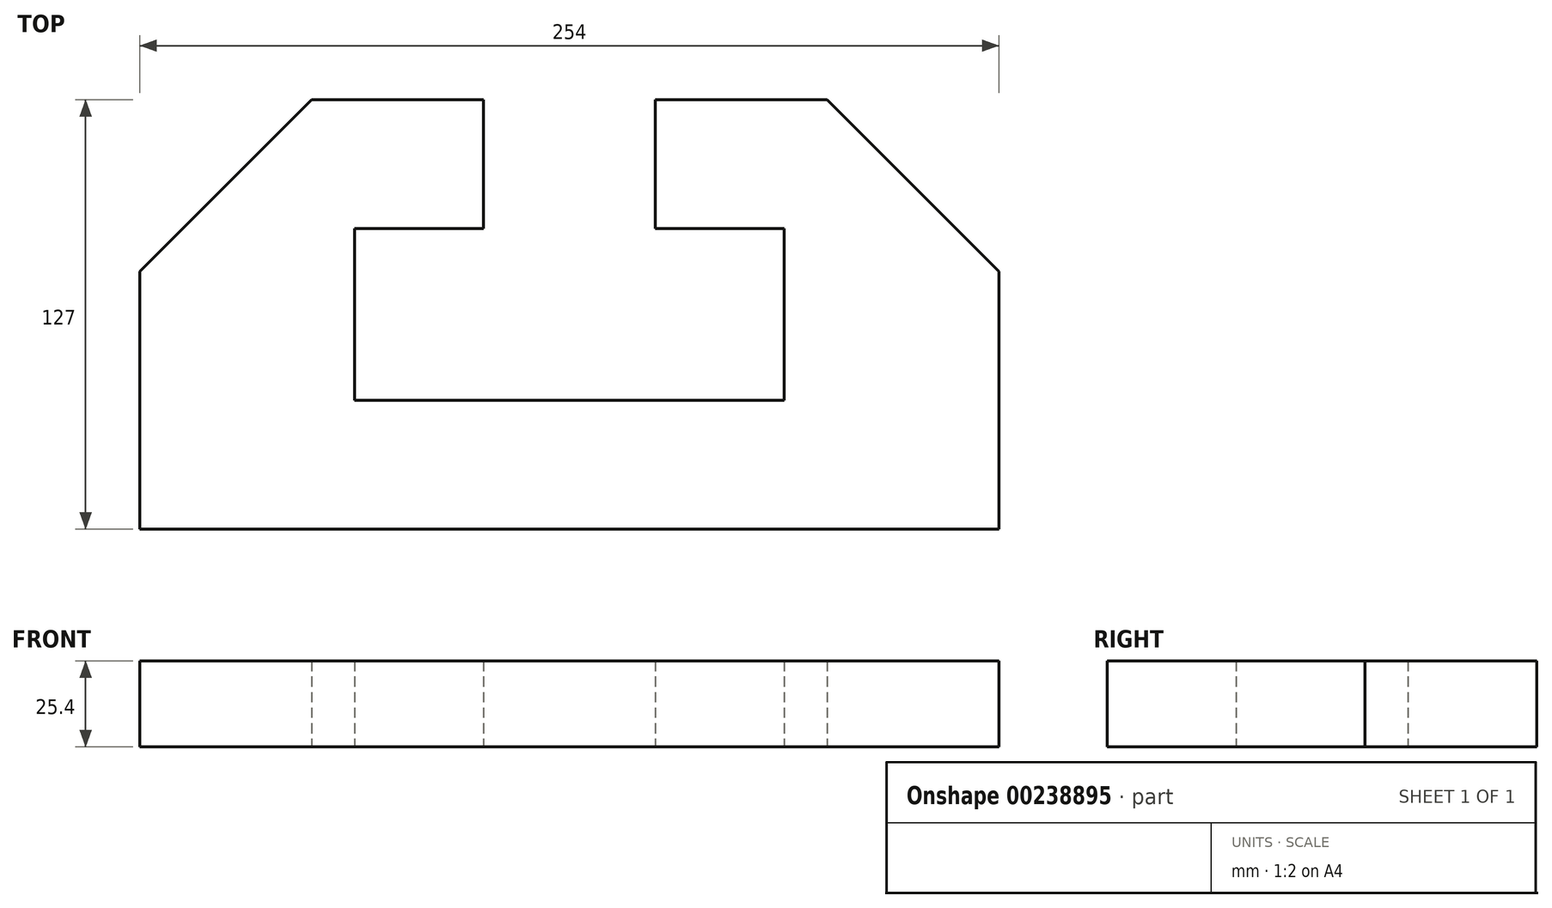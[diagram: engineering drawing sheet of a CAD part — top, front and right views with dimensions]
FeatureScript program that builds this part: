
annotation { "Feature Type Name" : "Feature", "Feature Type Description" : "" }
export const myFeature = defineFeature(function(context is Context, id is Id, definition is map)
    precondition{}
    {
        {
            var Q0;
            Q0=qCreatedBy(makeId("Top.planeOp"),FACE);
            var sketch = newSketch(context, id + "F0", { "sketchPlane" : qUnion([Q0])});
            skLineSegment(sketch, "E0", {"start": v(-152.4, -88.9) * mm, "end": v(101.6, -88.9) * mm});
            skLineSegment(sketch, "E1", {"start": v(-152.4, -88.9) * mm, "end": v(-152.4, -12.7) * mm});
            skLineSegment(sketch, "E2", {"start": v(-152.4, -12.7) * mm, "end": v(-101.6, 38.1) * mm});
            skLineSegment(sketch, "E3", {"start": v(-101.6, 38.1) * mm, "end": v(-50.8, 38.1) * mm});
            skLineSegment(sketch, "E4", {"start": v(-50.8, 38.1) * mm, "end": v(-50.8, 0) * mm});
            skLineSegment(sketch, "E5", {"start": v(-50.8, 0) * mm, "end": v(-88.9, 0) * mm});
            skLineSegment(sketch, "E6", {"start": v(-88.9, 0) * mm, "end": v(-88.9, -50.8) * mm});
            skLineSegment(sketch, "E7", {"start": v(-88.9, -50.8) * mm, "end": v(38.1, -50.8) * mm});
            skLineSegment(sketch, "E8", {"start": v(101.6, -88.9) * mm, "end": v(101.6, -12.7) * mm});
            skLineSegment(sketch, "E9", {"start": v(38.1, -50.8) * mm, "end": v(38.1, 0) * mm});
            skLineSegment(sketch, "E10", {"start": v(38.1, 0) * mm, "end": v(0, 0) * mm});
            skLineSegment(sketch, "E11", {"start": v(0, 0) * mm, "end": v(0, 38.1) * mm});
            skLineSegment(sketch, "E12", {"start": v(0, 38.1) * mm, "end": v(50.8, 38.1) * mm});
            skLineSegment(sketch, "E13", {"start": v(50.8, 38.1) * mm, "end": v(101.6, -12.7) * mm});
            skSolve(sketch);
        }
        {
            var Q0;
            Q0 = qSketchRegion(id + "F0", true);
            extrude(context, id + "F1", {"entities" : qUnion([Q0]), "depth" : 25.4 * mm});
        }
    });
